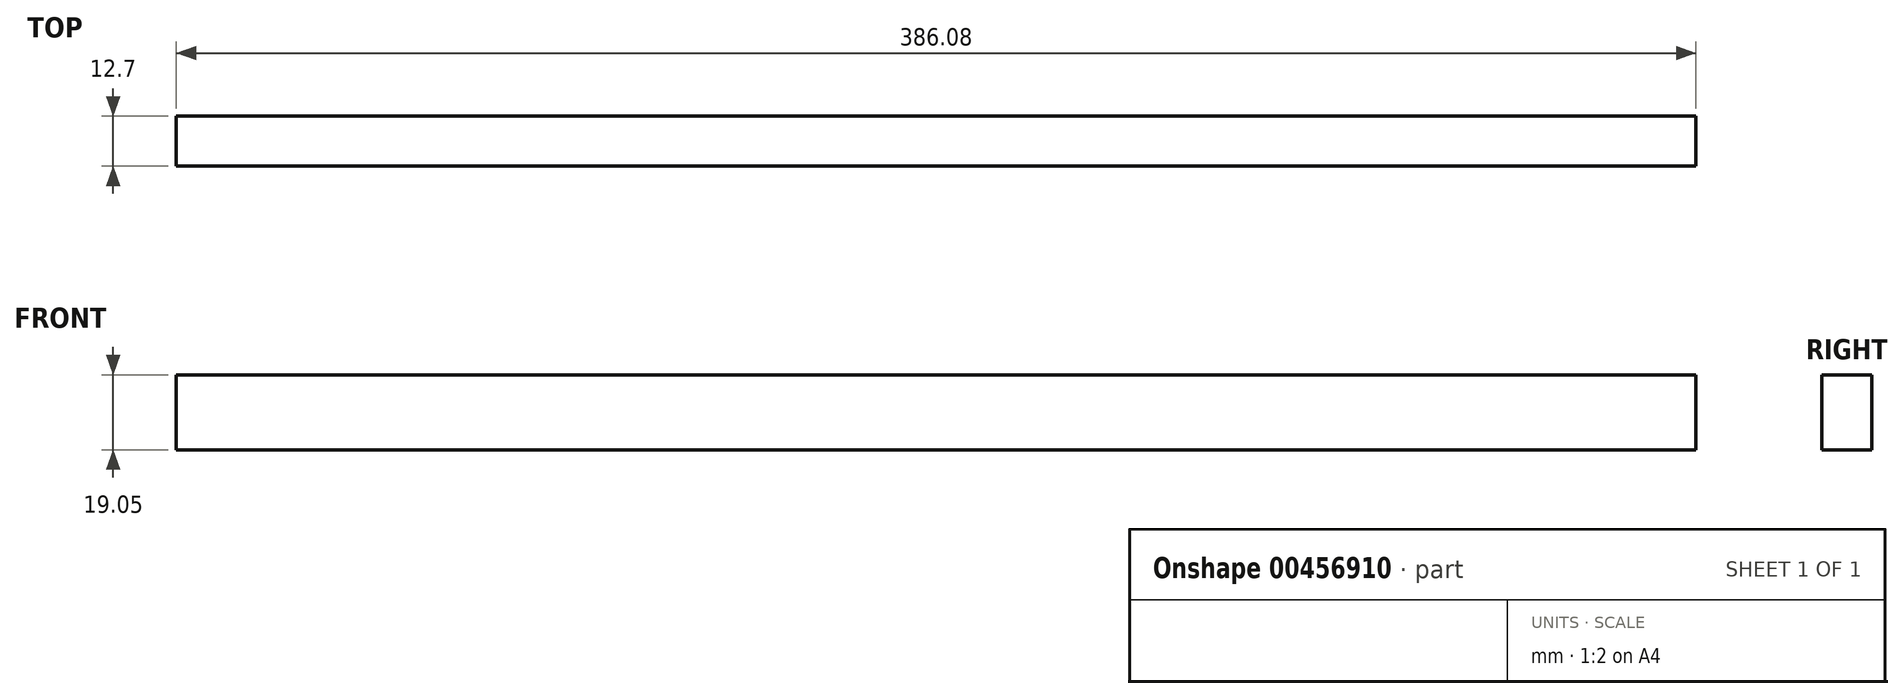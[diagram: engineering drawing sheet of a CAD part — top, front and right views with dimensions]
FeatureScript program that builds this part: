
annotation { "Feature Type Name" : "Feature", "Feature Type Description" : "" }
export const myFeature = defineFeature(function(context is Context, id is Id, definition is map)
    precondition{}
    {
        {
            var Q0;
            Q0=qCreatedBy(makeId("Front.planeOp"),FACE);
            var sketch = newSketch(context, id + "F0", { "sketchPlane" : qUnion([Q0])});
            skLineSegment(sketch, "E0.bottom", {"start": v(325.12, 154.51) * mm, "end": v(325.12, 135.46) * mm});
            skLineSegment(sketch, "E0.top", {"start": v(-60.96, 154.51) * mm, "end": v(-60.96, 135.46) * mm});
            skLineSegment(sketch, "E0.left", {"start": v(325.12, 154.51) * mm, "end": v(-60.96, 154.51) * mm});
            skLineSegment(sketch, "E0.right", {"start": v(325.12, 135.46) * mm, "end": v(-60.96, 135.46) * mm});
            skSolve(sketch);
        }
        {
            var Q0;
            Q0=makeQuery(id+"F0.imprint","IMPRINT",FACE,{"disambiguationData":[TD([[makeQuery(id+"F0.imprint","IMPRINT",EDGE,{"derivedFrom":sQuery(id+"F0.wireOp",EDGE,"CR0fLDGC-FUSB-T87a-WjLq-PKh2d8LQHOZw.bottom")}),-1.0]])]});
            var Q1;
            Q1=makeQuery(id+"F0.imprint","IMPRINT",FACE,{"disambiguationData":[TD([[makeQuery(id+"F0.imprint","IMPRINT",EDGE,{"derivedFrom":sQuery(id+"F0.wireOp",EDGE,"E0.bottom")}),-1.0]])]});
            extrude(context, id + "F1", {"entities" : qUnion([Q0, Q1]), "depth" : 12.7 * mm});
        }
    });
